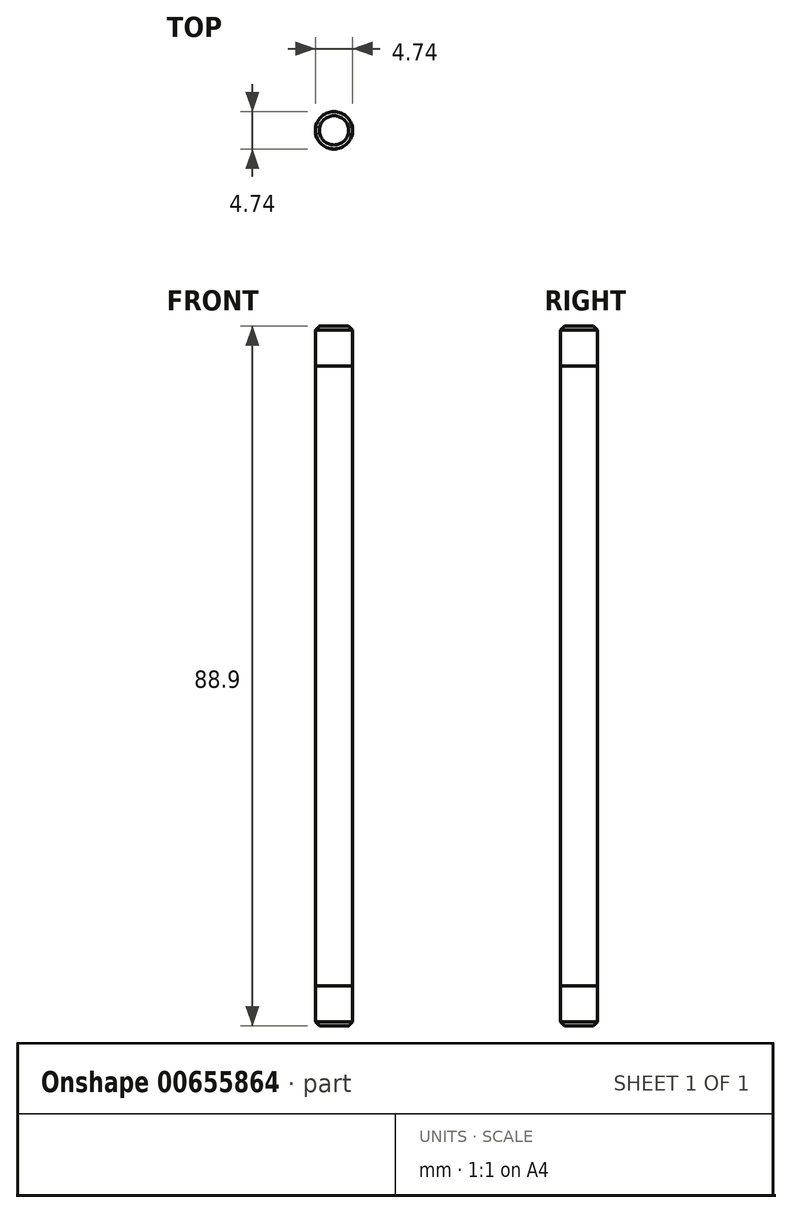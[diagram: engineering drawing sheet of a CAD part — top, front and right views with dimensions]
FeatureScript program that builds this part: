
annotation { "Feature Type Name" : "Feature", "Feature Type Description" : "" }
export const myFeature = defineFeature(function(context is Context, id is Id, definition is map)
    precondition{}
    {
        {
            var Q0;
            Q0=qCreatedBy(makeId("Front.planeOp"),FACE);
            var sketch = newSketch(context, id + "F0", { "sketchPlane" : qUnion([Q0])});
            skLineSegment(sketch, "E0", {"start": v(0, 0) * mm, "end": v(-2.36, 0) * mm});
            skLineSegment(sketch, "E1", {"start": v(-2.36, 0) * mm, "end": v(-2.36, 5.08) * mm});
            skLineSegment(sketch, "E2", {"start": v(-2.36, 5.08) * mm, "end": v(-2.37, 5.08) * mm});
            skLineSegment(sketch, "E3", {"start": v(-2.37, 5.08) * mm, "end": v(-2.37, 83.82) * mm});
            skLineSegment(sketch, "E4", {"start": v(-2.37, 83.82) * mm, "end": v(-2.36, 83.82) * mm});
            skLineSegment(sketch, "E5", {"start": v(-2.36, 83.82) * mm, "end": v(-2.36, 88.9) * mm});
            skLineSegment(sketch, "E6", {"start": v(-2.36, 88.9) * mm, "end": v(0, 88.9) * mm});
            skLineSegment(sketch, "E7", {"start": v(0, 88.9) * mm, "end": v(0, 0) * mm});
            skSolve(sketch);
        }
        {
            var Q0;
            Q0=makeQuery(id+"F0.imprint","IMPRINT",FACE,{"disambiguationData":[TD([[makeQuery(id+"F0.imprint","IMPRINT",EDGE,{"derivedFrom":sQuery(id+"F0.wireOp",EDGE,"E0")}),-1.0]])]});
            var Q1;
            Q1=sQuery(id+"F0.wireOp",EDGE,"E7");
            revolve(context, id + "F1", {"entities" : qUnion([Q0]), "axis" : qUnion([Q1]), "revolveType" : RevolveType.FULL});
        }
        {
            var Q0;
            Q0=makeQuery(id+"F1.opRevolve","SWEPT_FACE",FACE,{"disambiguationData":[OSD([sQuery(id+"F0.wireOp",EDGE,"E6")])]});
            var Q1;
            Q1=makeQuery(id+"F1.opRevolve","SWEPT_FACE",FACE,{"disambiguationData":[OSD([sQuery(id+"F0.wireOp",EDGE,"E0")])]});
            chamfer(context, id + "F2", {"entities" : qUnion([Q0, Q1]), "width" : 0.5 * mm, "tangentPropagation" : true});
        }
    });
